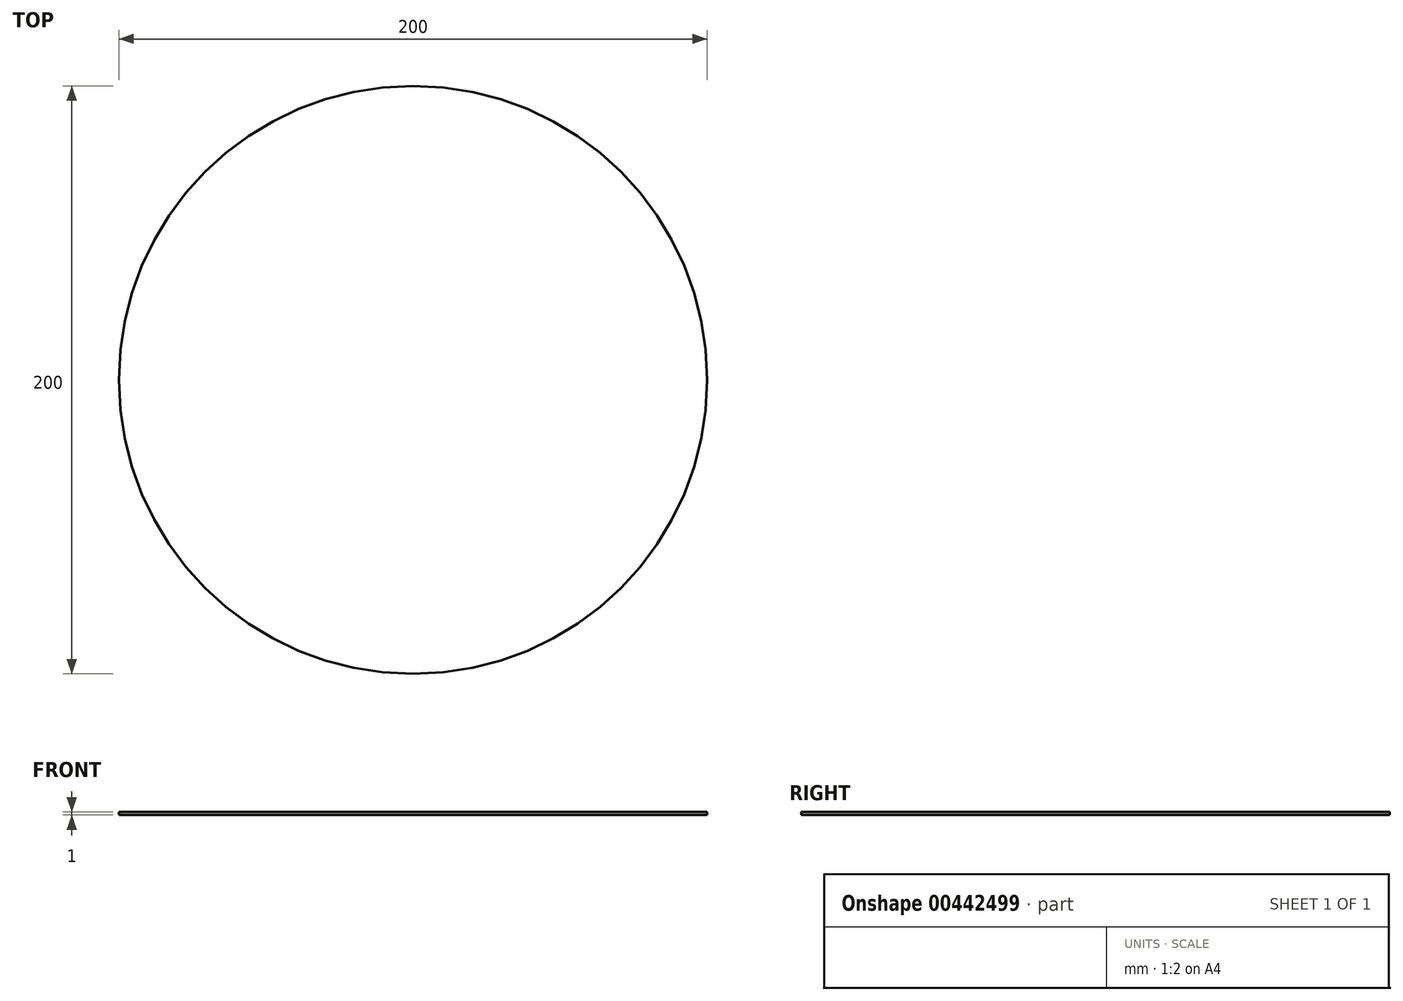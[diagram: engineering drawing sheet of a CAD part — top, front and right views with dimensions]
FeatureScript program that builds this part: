
annotation { "Feature Type Name" : "Feature", "Feature Type Description" : "" }
export const myFeature = defineFeature(function(context is Context, id is Id, definition is map)
    precondition{}
    {
        {
            var Q0;
            Q0=qCreatedBy(makeId("Top.planeOp"),FACE);
            var sketch = newSketch(context, id + "F0", { "sketchPlane" : qUnion([Q0])});
            skCircle(sketch, "E0", {"center": v(0, 0) * mm, "radius": 100 * mm});
            skSolve(sketch);
        }
        {
            var Q0;
            Q0 = qSketchRegion(id + "F0", true);
            extrude(context, id + "F1", {"entities" : qUnion([Q0]), "depth" : 1 * mm});
        }
    });
